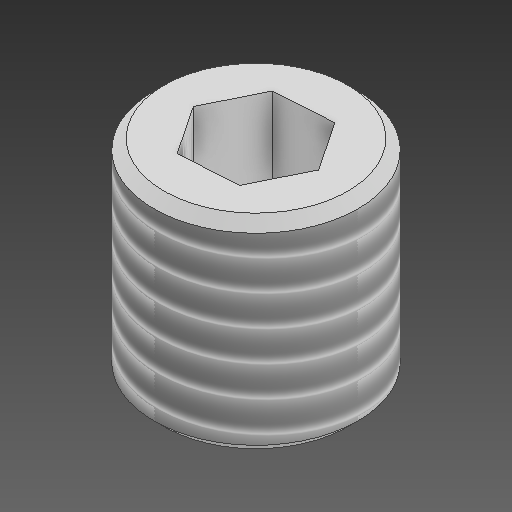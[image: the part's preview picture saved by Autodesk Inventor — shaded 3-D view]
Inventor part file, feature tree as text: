
AUTODESK INVENTOR PART (.ipt)
format: ipt  version: 2021 (Build 250183000, 183)  size: 179,712 bytes
history: native  units: mm
features: extrude x2, sketch x2, thread x1, chamfer x1
ambient origin geometry x8: Origin, YZ Plane, XZ Plane, XY Plane, X Axis, Y Axis, Z Axis, Center Point
bodies: Solid1 (feature_tree)
feature tree (6):
  extrude  "Extrusion1"  Depth=5.0mm
  extrude  "Extrusion2"  Depth=5.5mm TaperAngle=0.0deg
  thread  "Thread1"  [1 undecoded]
  chamfer  "Chamfer1"  Distance=0.5mm Angle=45.0deg
  sketch  "Sketch1"  dims[d0=10.0mm d1=0.0mm d2=5.0mm]
  sketch  "Sketch2"  dims[d3=10.0mm d4=5.5mm d5=0.0mm d6=10.0mm d7=0.0mm d8=0.5mm d9=2.0mm d10=45.0deg]
note: 1 required parameter value undecoded (feature->parameter linkage not recoverable at this tier; creation-order binding heuristic only, values carry confidence <= 0.55)
